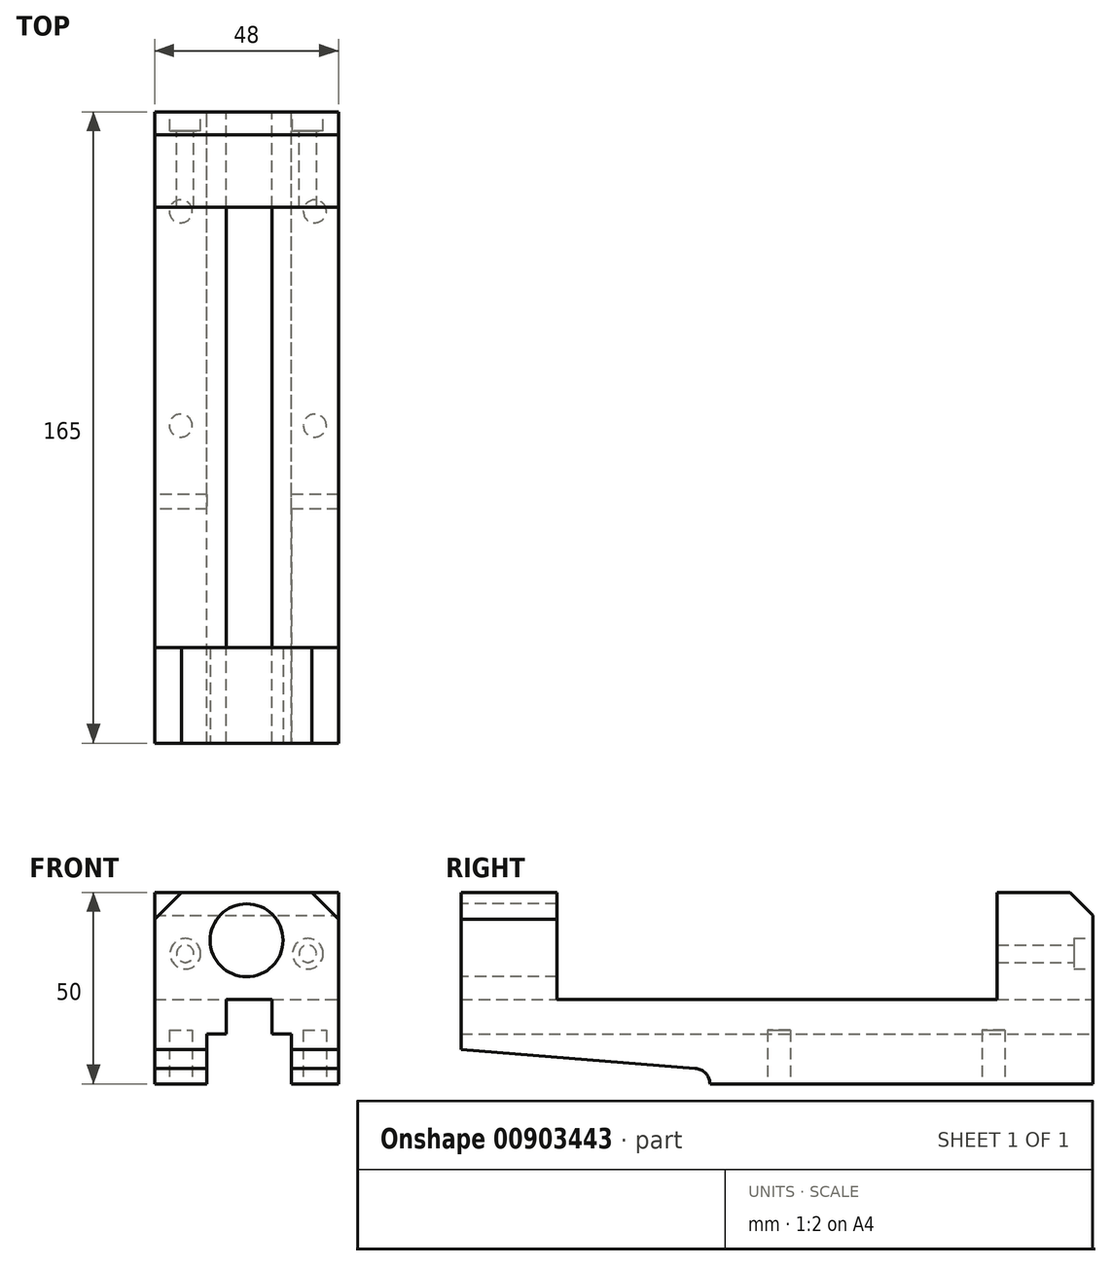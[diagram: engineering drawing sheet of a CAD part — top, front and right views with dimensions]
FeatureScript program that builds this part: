
annotation { "Feature Type Name" : "Feature", "Feature Type Description" : "" }
export const myFeature = defineFeature(function(context is Context, id is Id, definition is map)
    precondition{}
    {
        {
            var Q0;
            Q0=qCreatedBy(makeId("Top.planeOp"),FACE);
            var sketch = newSketch(context, id + "F0", { "sketchPlane" : qUnion([Q0])});
            skLineSegment(sketch, "E0.bottom", {"start": v(24, 82.5) * mm, "end": v(-24, 82.5) * mm});
            skLineSegment(sketch, "E0.top", {"start": v(24, -82.5) * mm, "end": v(-24, -82.5) * mm});
            skLineSegment(sketch, "E0.left", {"start": v(24, 82.5) * mm, "end": v(24, -82.5) * mm});
            skLineSegment(sketch, "E0.right", {"start": v(-24, 82.5) * mm, "end": v(-24, -82.5) * mm});
            skPoint(sketch, "E0.middle", {"position": v(0, 0) * mm});
            skSolve(sketch);
        }
        {
            var Q0;
            Q0 = qSketchRegion(id + "F0", true);
            extrude(context, id + "F1", {"entities" : qUnion([Q0]), "depth" : 50 * mm, "offsetDistance" : 25 * mm});
        }
        {
            var Q0;
            Q0=makeQuery(id+"F1.opExtrude","SWEPT_FACE",FACE,{"disambiguationData":[OSD([sQuery(id+"F0.wireOp",EDGE,"E0.left")])]});
            var sketch = newSketch(context, id + "F2", { "sketchPlane" : qUnion([Q0])});
            skLineSegment(sketch, "E1.bottom", {"start": v(-57.5, 50) * mm, "end": v(57.5, 50) * mm});
            skLineSegment(sketch, "E1.top", {"start": v(-57.5, 22) * mm, "end": v(57.5, 22) * mm});
            skLineSegment(sketch, "E1.left", {"start": v(-57.5, 50) * mm, "end": v(-57.5, 22) * mm});
            skLineSegment(sketch, "E1.right", {"start": v(57.5, 50) * mm, "end": v(57.5, 22) * mm});
            skSolve(sketch);
        }
        {
            var Q0;
            Q0=makeQuery(id+"F2.imprint","IMPRINT",FACE,{"disambiguationData":[TD([[makeQuery(id+"F2.imprint","IMPRINT",EDGE,{"derivedFrom":sQuery(id+"F2.wireOp",EDGE,"E1.bottom")}),1.0]])]});
            extrude(context, id + "F3", {"entities" : qUnion([Q0]), "operationType" : NewBodyOperationType.REMOVE, "oppositeDirection" : true, "depth" : 48 * mm, "offsetDistance" : 25 * mm});
        }
        {
            var Q0;
            Q0=makeQuery(id+"F1.opExtrude","SWEPT_FACE",FACE,{"disambiguationData":[OSD([sQuery(id+"F0.wireOp",EDGE,"E0.top")])]});
            var sketch = newSketch(context, id + "F4", { "sketchPlane" : qUnion([Q0])});
            skCircle(sketch, "E2", {"center": v(0, 37.5) * mm, "radius": 9.53 * mm});
            skSolve(sketch);
        }
        {
            var Q0;
            Q0=makeQuery(id+"F4.imprint","IMPRINT",FACE,{"disambiguationData":[TD([[makeQuery(id+"F4.imprint","IMPRINT",EDGE,{"derivedFrom":sQuery(id+"F4.wireOp",EDGE,"E2")}),1.0]])]});
            var Q1;
            Q1=sQuery(id+"F4.wireOp",EDGE,"E2");
            extrude(context, id + "F5", {"entities" : qUnion([Q0]), "operationType" : NewBodyOperationType.REMOVE, "surfaceEntities" : qUnion([Q1]), "oppositeDirection" : true, "depth" : 25 * mm, "offsetDistance" : 25 * mm});
        }
        {
            var Q0;
            {var subQ0=sQuery(id+"F0.wireOp",EDGE,"E0.right");var subQ1=sQuery(id+"F0.wireOp",EDGE,"E0.top");Q0=makeQuery(id+"F3.boolean.opBoolean","SPLIT",EDGE,{"disambiguationData":[TD([makeQuery(id+"F1.opExtrude","SWEPT_FACE",FACE,{"disambiguationData":[OSD([subQ1])]})])],"derivedFrom":makeQuery(id+"F1.opExtrude","CAP_EDGE",EDGE,{"disambiguationData":[OSD([subQ0])],"isStart":false})});}
            var Q1;
            {var subQ0=sQuery(id+"F0.wireOp",EDGE,"E0.left");var subQ1=sQuery(id+"F0.wireOp",EDGE,"E0.top");Q1=makeQuery(id+"F3.boolean.opBoolean","SPLIT",EDGE,{"disambiguationData":[TD([makeQuery(id+"F1.opExtrude","SWEPT_FACE",FACE,{"disambiguationData":[OSD([subQ1])]})])],"derivedFrom":makeQuery(id+"F1.opExtrude","CAP_EDGE",EDGE,{"disambiguationData":[OSD([subQ0])],"isStart":false})});}
            chamfer(context, id + "F6", {"entities" : qUnion([Q0, Q1]), "width" : 7 * mm, "tangentPropagation" : true});
        }
        {
            var Q0;
            Q0=makeQuery(id+"F1.opExtrude","CAP_EDGE",EDGE,{"disambiguationData":[OSD([sQuery(id+"F0.wireOp",EDGE,"E0.bottom")])],"isStart":false});
            chamfer(context, id + "F7", {"entities" : qUnion([Q0]), "width" : 6 * mm, "tangentPropagation" : true});
        }
        {
            var Q0;
            Q0=makeQuery(id+"F1.opExtrude","SWEPT_FACE",FACE,{"disambiguationData":[OSD([sQuery(id+"F0.wireOp",EDGE,"E0.bottom")])]});
            var sketch = newSketch(context, id + "F8", { "sketchPlane" : qUnion([Q0])});
            skLineSegment(sketch, "E3", {"start": v(0, 0) * mm, "end": v(-11.68, 0) * mm});
            skLineSegment(sketch, "E4", {"start": v(-11.68, 0) * mm, "end": v(-11.68, 13) * mm});
            skLineSegment(sketch, "E5", {"start": v(-11.68, 13) * mm, "end": v(-6.68, 13) * mm});
            skLineSegment(sketch, "E6", {"start": v(-6.68, 13) * mm, "end": v(-6.68, 22) * mm});
            skLineSegment(sketch, "E7", {"start": v(-6.68, 22) * mm, "end": v(5.37, 22) * mm});
            skLineSegment(sketch, "E8", {"start": v(5.37, 22) * mm, "end": v(5.37, 13) * mm});
            skLineSegment(sketch, "E9", {"start": v(5.37, 13) * mm, "end": v(10.37, 13) * mm});
            skLineSegment(sketch, "E10", {"start": v(10.37, 13) * mm, "end": v(10.37, 0) * mm});
            skLineSegment(sketch, "E11", {"start": v(10.37, 0) * mm, "end": v(0, 0) * mm});
            skSolve(sketch);
        }
        {
            var Q0;
            Q0=makeQuery(id+"F8.imprint","IMPRINT",FACE,{"disambiguationData":[TD([[makeQuery(id+"F8.imprint","IMPRINT",EDGE,{"derivedFrom":sQuery(id+"F8.wireOp",EDGE,"E3")}),1.0]])]});
            extrude(context, id + "F9", {"entities" : qUnion([Q0]), "operationType" : NewBodyOperationType.REMOVE, "oppositeDirection" : true, "depth" : 165 * mm, "offsetDistance" : 25 * mm});
        }
        {
            var Q0;
            {var subQ4=sQuery(id+"F8.wireOp",EDGE,"E4");Q0=makeQuery(id+"F8.imprint","IMPRINT",FACE,{"disambiguationData":[TD([[makeQuery(id+"F8.imprint","IMPRINT",EDGE,{"derivedFrom":subQ4}),1.0]])]});}
            var sketch = newSketch(context, id + "F10", { "sketchPlane" : qUnion([Q0])});
            skCircle(sketch, "E12", {"center": v(-16, 34) * mm, "radius": 2.25 * mm});
            skCircle(sketch, "E13", {"center": v(16, 34) * mm, "radius": 2.25 * mm});
            skCircle(sketch, "E14", {"center": v(-16, 34) * mm, "radius": 4 * mm});
            skCircle(sketch, "E15", {"center": v(16, 34) * mm, "radius": 4 * mm});
            skSolve(sketch);
        }
        {
            var Q0;
            Q0=makeQuery(id+"F10.imprint","IMPRINT",FACE,{"disambiguationData":[TD([[makeQuery(id+"F10.imprint","IMPRINT",EDGE,{"derivedFrom":sQuery(id+"F10.wireOp",EDGE,"E13")}),1.0]])]});
            var Q1;
            Q1=makeQuery(id+"F10.imprint","IMPRINT",FACE,{"disambiguationData":[TD([[makeQuery(id+"F10.imprint","IMPRINT",EDGE,{"derivedFrom":sQuery(id+"F10.wireOp",EDGE,"E12")}),1.0]])]});
            var Q2;
            Q2=sQuery(id+"F10.wireOp",EDGE,"E13");
            var Q3;
            Q3=sQuery(id+"F10.wireOp",EDGE,"E12");
            extrude(context, id + "F11", {"entities" : qUnion([Q0, Q1]), "operationType" : NewBodyOperationType.REMOVE, "surfaceEntities" : qUnion([Q2, Q3]), "oppositeDirection" : true, "depth" : 25 * mm, "offsetDistance" : 25 * mm});
        }
        {
            var Q0;
            Q0=makeQuery(id+"F10.imprint","IMPRINT",FACE,{"disambiguationData":[TD([[makeQuery(id+"F10.imprint","IMPRINT",EDGE,{"derivedFrom":sQuery(id+"F10.wireOp",EDGE,"E12")}),-1.0]])]});
            var Q1;
            Q1=makeQuery(id+"F10.imprint","IMPRINT",FACE,{"disambiguationData":[TD([[makeQuery(id+"F10.imprint","IMPRINT",EDGE,{"derivedFrom":sQuery(id+"F10.wireOp",EDGE,"E13")}),-1.0]])]});
            var Q2;
            Q2=sQuery(id+"F10.wireOp",EDGE,"E14");
            var Q3;
            Q3=sQuery(id+"F10.wireOp",EDGE,"E15");
            extrude(context, id + "F12", {"entities" : qUnion([Q0, Q1]), "operationType" : NewBodyOperationType.REMOVE, "surfaceEntities" : qUnion([Q2, Q3]), "oppositeDirection" : true, "depth" : 5 * mm, "offsetDistance" : 25 * mm});
        }
        {
            var Q0;
            Q0=makeQuery(id+"F1.opExtrude","SWEPT_FACE",FACE,{"disambiguationData":[OSD([sQuery(id+"F0.wireOp",EDGE,"E0.right")])]});
            var sketch = newSketch(context, id + "F13", { "sketchPlane" : qUnion([Q0])});
            skArc(sketch, "E16", {"start": v(21.37, 4) * mm, "mid": v(18.63, 2.78) * mm, "end": v(17.5, 0) * mm});
            skLineSegment(sketch, "E17", {"start": v(21.37, 4) * mm, "end": v(82.5, 9) * mm});
            skLineSegment(sketch, "E18", {"start": v(82.5, 9) * mm, "end": v(82.5, 0) * mm});
            skLineSegment(sketch, "E19", {"start": v(17.5, 0) * mm, "end": v(82.5, 0) * mm});
            skSolve(sketch);
        }
        {
            var Q0;
            Q0=makeQuery(id+"F13.imprint","IMPRINT",FACE,{"disambiguationData":[TD([[makeQuery(id+"F13.imprint","IMPRINT",EDGE,{"derivedFrom":sQuery(id+"F13.wireOp",EDGE,"E16")}),1.0]])]});
            extrude(context, id + "F14", {"entities" : qUnion([Q0]), "operationType" : NewBodyOperationType.REMOVE, "oppositeDirection" : true, "depth" : 48 * mm, "offsetDistance" : 25 * mm});
        }
        {
            var Q0;
            {var subQ0=sQuery(id+"F0.wireOp",EDGE,"E0.bottom");var subQ1=sQuery(id+"F0.wireOp",EDGE,"E0.right");var subQ2=sQuery(id+"F0.wireOp",EDGE,"E0.top");Q0=makeQuery(id+"F9.boolean.opBoolean","SPLIT",FACE,{"disambiguationData":[TD([makeQuery(id+"F1.opExtrude","SWEPT_FACE",FACE,{"disambiguationData":[OSD([subQ1])]})])],"derivedFrom":makeQuery(id+"F1.opExtrude","CAP_FACE",FACE,{"disambiguationData":[OSD([subQ0,subQ2,sQuery(id+"F0.wireOp",EDGE,"E0.left"),subQ1])],"isStart":true})});}
            var sketch = newSketch(context, id + "F15", { "sketchPlane" : qUnion([Q0])});
            skCircle(sketch, "E20", {"center": v(-17.18, -56.5) * mm, "radius": 3 * mm});
            skPoint(sketch, "E20.centerSnap0", {"position": v(-17.18, -82.5) * mm});
            skCircle(sketch, "E21", {"center": v(17.82, -56.5) * mm, "radius": 3 * mm});
            skCircle(sketch, "E22", {"center": v(-17.18, -0.5) * mm, "radius": 3 * mm});
            skCircle(sketch, "E23", {"center": v(17.82, -0.5) * mm, "radius": 3 * mm});
            skSolve(sketch);
        }
        {
            var Q0;
            Q0=makeQuery(id+"F15.imprint","IMPRINT",FACE,{"disambiguationData":[TD([[makeQuery(id+"F15.imprint","IMPRINT",EDGE,{"derivedFrom":sQuery(id+"F15.wireOp",EDGE,"E22")}),1.0]])]});
            var Q1;
            Q1=makeQuery(id+"F15.imprint","IMPRINT",FACE,{"disambiguationData":[TD([[makeQuery(id+"F15.imprint","IMPRINT",EDGE,{"derivedFrom":sQuery(id+"F15.wireOp",EDGE,"E20")}),1.0]])]});
            var Q2;
            Q2=makeQuery(id+"F15.imprint","IMPRINT",FACE,{"disambiguationData":[TD([[makeQuery(id+"F15.imprint","IMPRINT",EDGE,{"derivedFrom":sQuery(id+"F15.wireOp",EDGE,"E21")}),1.0]])]});
            var Q3;
            Q3=makeQuery(id+"F15.imprint","IMPRINT",FACE,{"disambiguationData":[TD([[makeQuery(id+"F15.imprint","IMPRINT",EDGE,{"derivedFrom":sQuery(id+"F15.wireOp",EDGE,"E23")}),1.0]])]});
            var Q4;
            Q4=sQuery(id+"F15.wireOp",EDGE,"E22");
            var Q5;
            Q5=sQuery(id+"F15.wireOp",EDGE,"E20");
            var Q6;
            Q6=sQuery(id+"F15.wireOp",EDGE,"E21");
            var Q7;
            Q7=sQuery(id+"F15.wireOp",EDGE,"E23");
            extrude(context, id + "F16", {"entities" : qUnion([Q0, Q1, Q2, Q3]), "operationType" : NewBodyOperationType.REMOVE, "surfaceEntities" : qUnion([Q4, Q5, Q6, Q7]), "oppositeDirection" : true, "depth" : 14 * mm, "offsetDistance" : 25 * mm});
        }
    });
